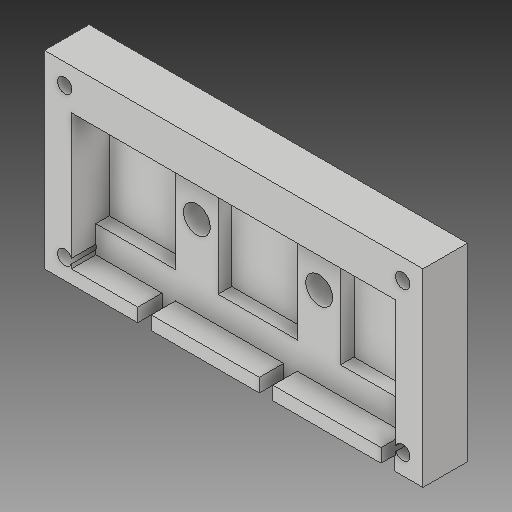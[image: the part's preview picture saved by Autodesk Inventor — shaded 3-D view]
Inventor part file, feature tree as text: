
AUTODESK INVENTOR PART (.ipt)
format: ipt  version: 2018 (Build 220112000, 112)  size: 231,424 bytes
history: native  units: in
note: dims shown in document units (in); Inventor stores cm internally (conversion verified against a paired STEP export)
features: extrude x5, sketch x4, hole x2, pattern_linear x1, projected_geometry x1
ambient origin geometry x8: Origin, YZ Plane, XZ Plane, XY Plane, X Axis, Y Axis, Z Axis, Center Point
bodies: Solid1 (feature_tree)
feature tree (13):
  sketch  "Sketch1"  dims[d0=7.0in d1=3.5in]
  extrude  "Extrusion1"  Depth=3.5in
  extrude  "Extrusion2"  Depth=2.0in
  extrude  "Extrusion3"  Depth=0.5in
  extrude  "Extrusion4"  Depth=0.7in TaperAngle=0.0deg
  pattern_linear  "Rectangular Pattern1"  Spacing1=0.125in  [1 undecoded]
  hole  "Hole2"  [1 undecoded]
  extrude  "Extrusion5"  Depth=0.25in
  sketch  "Sketch2"  dims[d2=1.475in d3=2.0in]
  sketch  "Sketch3"  dims[d4=0.5in d5=0.5in]
  hole  "Hole1"  [1 undecoded]
  sketch  "Sketch4"  dims[d6=0.5in d7=0.7in d8=0.0in d9=0.125in d10=0.0in d11=0.25in d12=0.0in d13=0.25in d14=0.25in d15=0.0in d16=1.1811in d18=2.25in d19=0.266in d20=0.75in d21=0.375in d22=0.25in d23=0.5635in d24=1.0in d25=0.0in d26=0.5in d27=1.0in d28=0.0in]
  projected_geometry  "Projected Loop1"
note: 3 required parameter values undecoded (feature->parameter linkage not recoverable at this tier; creation-order binding heuristic only, values carry confidence <= 0.55)
